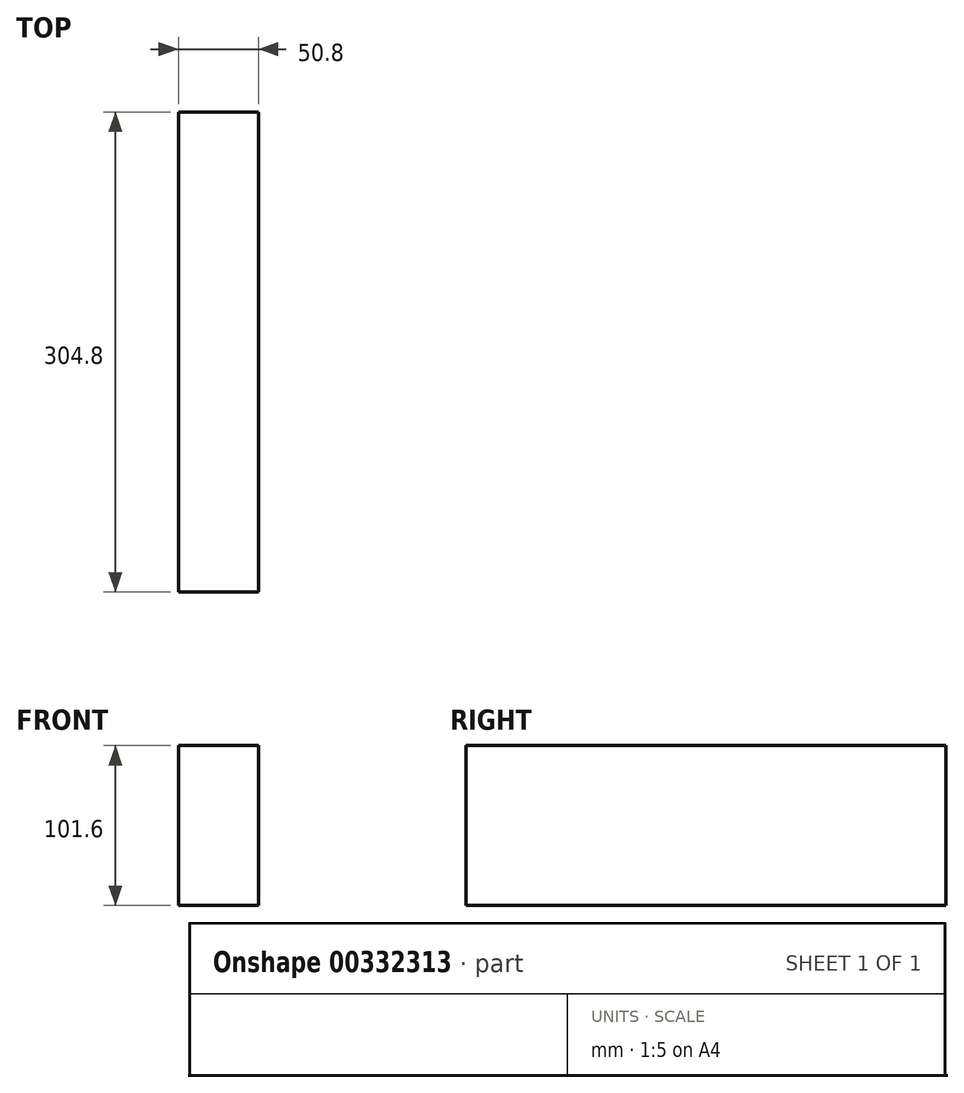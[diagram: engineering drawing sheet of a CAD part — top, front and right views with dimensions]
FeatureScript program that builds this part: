
annotation { "Feature Type Name" : "Feature", "Feature Type Description" : "" }
export const myFeature = defineFeature(function(context is Context, id is Id, definition is map)
    precondition{}
    {
        {
            var Q0;
            Q0=qCreatedBy(makeId("Right.planeOp"),FACE);
            var sketch = newSketch(context, id + "F0", { "sketchPlane" : qUnion([Q0])});
            skLineSegment(sketch, "E0.bottom", {"start": v(-801.9, -71.61) * mm, "end": v(-497.1, -71.61) * mm});
            skLineSegment(sketch, "E0.top", {"start": v(-801.9, -173.21) * mm, "end": v(-497.1, -173.21) * mm});
            skLineSegment(sketch, "E0.left", {"start": v(-801.9, -71.61) * mm, "end": v(-801.9, -173.21) * mm});
            skLineSegment(sketch, "E0.right", {"start": v(-497.1, -71.61) * mm, "end": v(-497.1, -173.21) * mm});
            skSolve(sketch);
        }
        {
            var Q0;
            Q0 = qSketchRegion(id + "F0", true);
            extrude(context, id + "F1", {"entities" : qUnion([Q0]), "depth" : 50.8 * mm});
        }
    });
